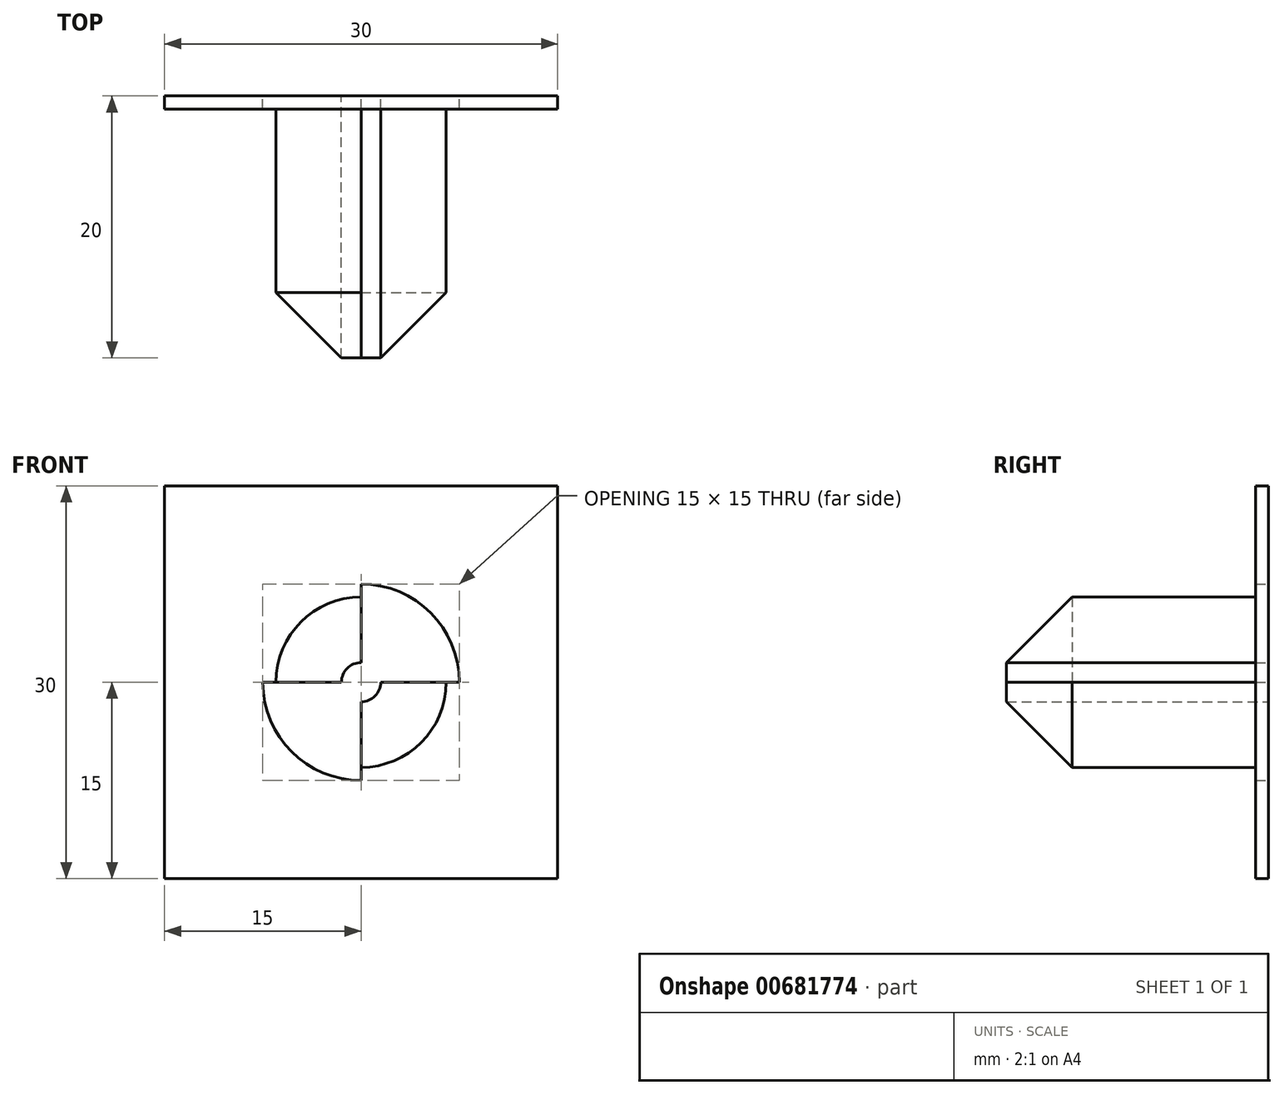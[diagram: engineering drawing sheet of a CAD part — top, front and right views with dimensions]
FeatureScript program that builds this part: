
annotation { "Feature Type Name" : "Feature", "Feature Type Description" : "" }
export const myFeature = defineFeature(function(context is Context, id is Id, definition is map)
    precondition{}
    {
        {
            var Q0;
            Q0=qCreatedBy(makeId("Front.planeOp"),FACE);
            var sketch = newSketch(context, id + "F0", { "sketchPlane" : qUnion([Q0])});
            skCircle(sketch, "E0", {"center": v(0, 0) * mm, "radius": 6.5 * mm});
            skSolve(sketch);
        }
        {
            var Q0;
            Q0 = qSketchRegion(id + "F0", true);
            extrude(context, id + "F1", {"entities" : qUnion([Q0]), "depth" : 20 * mm, "offsetDistance" : 25 * mm});
        }
        {
            var Q0;
            Q0=makeQuery(id+"F1.opExtrude","CAP_EDGE",EDGE,{"disambiguationData":[OSD([sQuery(id+"F0.wireOp",EDGE,"E0")])],"isStart":false});
            chamfer(context, id + "F2", {"entities" : qUnion([Q0]), "width" : 5 * mm, "tangentPropagation" : true});
        }
        {
            var Q0;
            Q0=qCreatedBy(makeId("Front.planeOp"),FACE);
            var sketch = newSketch(context, id + "F3", { "sketchPlane" : qUnion([Q0])});
            skLineSegment(sketch, "E1.bottom", {"start": v(15, -15) * mm, "end": v(-15, -15) * mm});
            skLineSegment(sketch, "E1.top", {"start": v(15, 15) * mm, "end": v(-15, 15) * mm});
            skLineSegment(sketch, "E1.left", {"start": v(15, -15) * mm, "end": v(15, 15) * mm});
            skLineSegment(sketch, "E1.right", {"start": v(-15, -15) * mm, "end": v(-15, 15) * mm});
            skSolve(sketch);
        }
        {
            var Q0;
            Q0 = qSketchRegion(id + "F3", true);
            extrude(context, id + "F4", {"entities" : qUnion([Q0]), "operationType" : NewBodyOperationType.ADD, "depth" : 1 * mm, "offsetDistance" : 25 * mm});
        }
        {
            var Q0;
            Q0=qCreatedBy(makeId("Front.planeOp"),FACE);
            var sketch = newSketch(context, id + "F5", { "sketchPlane" : qUnion([Q0])});
            skArc(sketch, "E2", {"start": v(-7.5, 0) * mm, "mid": v(-5.3, -5.3) * mm, "end": v(0, -7.5) * mm});
            skLineSegment(sketch, "E3", {"start": v(0, 7.5) * mm, "end": v(0, 1.5) * mm});
            skLineSegment(sketch, "E4", {"start": v(-1.5, 0) * mm, "end": v(-7.5, 0) * mm});
            skArc(sketch, "E5", {"start": v(0, 1.5) * mm, "mid": v(-1.06, 1.06) * mm, "end": v(-1.5, 0) * mm});
            skLineSegment(sketch, "E6", {"start": v(0, -1.5) * mm, "end": v(0, -7.5) * mm});
            skLineSegment(sketch, "E7", {"start": v(0, -7.5) * mm, "end": v(0, -1.5) * mm});
            skLineSegment(sketch, "E8", {"start": v(7.5, 0) * mm, "end": v(1.5, 0) * mm});
            skArc(sketch, "E9.trimOffspring", {"start": v(0, -1.5) * mm, "mid": v(1.06, -1.06) * mm, "end": v(1.5, 0) * mm});
            skArc(sketch, "E10.trimOffspring", {"start": v(7.5, 0) * mm, "mid": v(5.3, 5.3) * mm, "end": v(0, 7.5) * mm});
            skSolve(sketch);
        }
        {
            var Q0;
            Q0 = qSketchRegion(id + "F5", true);
            extrude(context, id + "F6", {"entities" : qUnion([Q0]), "operationType" : NewBodyOperationType.REMOVE, "depth" : 25 * mm, "offsetDistance" : 25 * mm});
        }
    });
